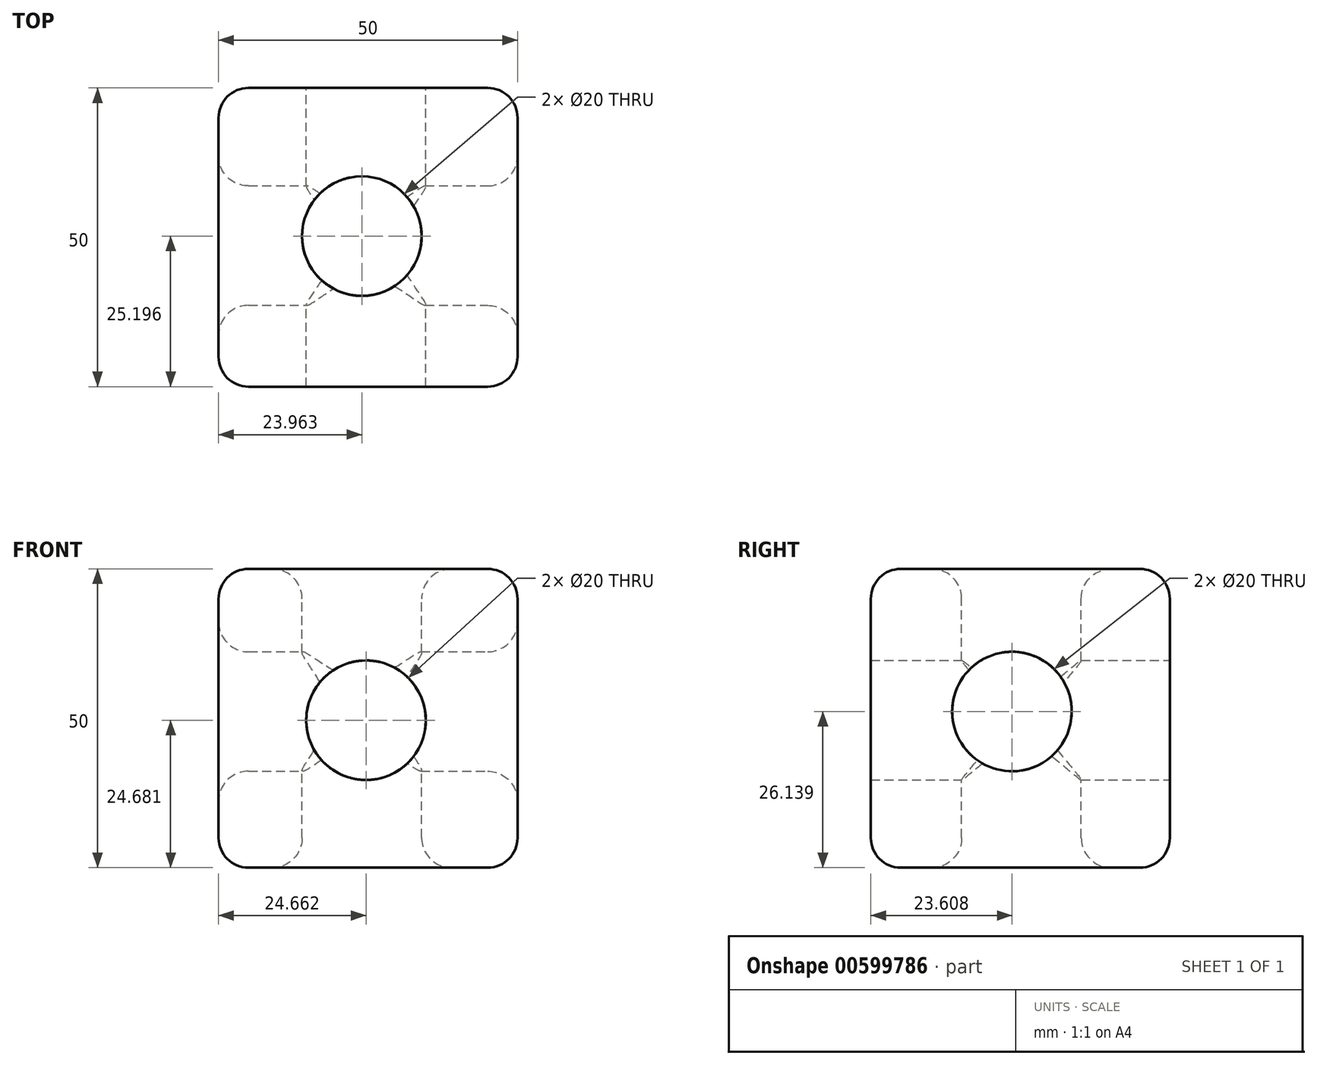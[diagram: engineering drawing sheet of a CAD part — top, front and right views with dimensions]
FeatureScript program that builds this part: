
annotation { "Feature Type Name" : "Feature", "Feature Type Description" : "" }
export const myFeature = defineFeature(function(context is Context, id is Id, definition is map)
    precondition{}
    {
        {
            var Q0;
            Q0=qCreatedBy(makeId("Top.planeOp"),FACE);
            var sketch = newSketch(context, id + "F0", { "sketchPlane" : qUnion([Q0])});
            skLineSegment(sketch, "E0.bottom", {"start": v(0, 0) * mm, "end": v(-50, 0) * mm});
            skLineSegment(sketch, "E0.top", {"start": v(0, -50) * mm, "end": v(-50, -50) * mm});
            skLineSegment(sketch, "E0.left", {"start": v(0, 0) * mm, "end": v(0, -50) * mm});
            skLineSegment(sketch, "E0.right", {"start": v(-50, 0) * mm, "end": v(-50, -50) * mm});
            skCircle(sketch, "E1", {"center": v(-26.04, -24.8) * mm, "radius": 10 * mm});
            skSolve(sketch);
        }
        {
            var Q0;
            Q0=makeQuery(id+"F0.imprint","IMPRINT",FACE,{"disambiguationData":[TD([[makeQuery(id+"F0.imprint","IMPRINT",EDGE,{"derivedFrom":sQuery(id+"F0.wireOp",EDGE,"E0.bottom")}),1.0]])]});
            extrude(context, id + "F1", {"entities" : qUnion([Q0]), "oppositeDirection" : true, "depth" : 50 * mm, "offsetDistance" : 25 * mm});
        }
        {
            var Q0;
            Q0=makeQuery(id+"F1.opExtrude","SWEPT_FACE",FACE,{"disambiguationData":[OSD([sQuery(id+"F0.wireOp",EDGE,"E0.bottom")])]});
            var sketch = newSketch(context, id + "F2", { "sketchPlane" : qUnion([Q0])});
            skCircle(sketch, "E2", {"center": v(25.34, -25.32) * mm, "radius": 10 * mm});
            skSolve(sketch);
        }
        {
            var Q0;
            Q0=sQuery(id+"F2.wireOp",VERTEX,"E2.center");
            var Q1;
            Q1=makeQuery(id+"F1.opExtrude","SWEPT_BODY",BODY,{"disambiguationData":[OSD([sQuery(id+"F0.wireOp",EDGE,"E0.bottom"),sQuery(id+"F0.wireOp",EDGE,"E0.top"),sQuery(id+"F0.wireOp",EDGE,"E0.left"),sQuery(id+"F0.wireOp",EDGE,"E0.right"),sQuery(id+"F0.wireOp",EDGE,"E1")])]});
            hole(context, id + "F3", {"style" : HoleStyle.SIMPLE, "endStyle" : HoleEndStyle.THROUGH, "holeDiameter" : 20 * mm, "majorDiameter" : 5 * mm, "isTappedThrough" : true, "tappedDepth" : 12.7 * mm, "tapClearance" : 3, "locations" : qUnion([Q0]), "scope" : qUnion([Q1])});
        }
        {
            var Q0;
            Q0=makeQuery(id+"F1.opExtrude","SWEPT_FACE",FACE,{"disambiguationData":[OSD([sQuery(id+"F0.wireOp",EDGE,"E0.left")])]});
            var sketch = newSketch(context, id + "F4", { "sketchPlane" : qUnion([Q0])});
            skCircle(sketch, "E3", {"center": v(-26.4, -23.86) * mm, "radius": 10 * mm});
            skSolve(sketch);
        }
        {
            var Q0;
            Q0=sQuery(id+"F4.wireOp",VERTEX,"E3.center");
            var Q1;
            Q1=makeQuery(id+"F1.opExtrude","SWEPT_BODY",BODY,{"disambiguationData":[OSD([sQuery(id+"F0.wireOp",EDGE,"E0.bottom"),sQuery(id+"F0.wireOp",EDGE,"E0.top"),sQuery(id+"F0.wireOp",EDGE,"E0.left"),sQuery(id+"F0.wireOp",EDGE,"E0.right"),sQuery(id+"F0.wireOp",EDGE,"E1")])]});
            hole(context, id + "F5", {"style" : HoleStyle.SIMPLE, "endStyle" : HoleEndStyle.THROUGH, "holeDiameter" : 20 * mm, "majorDiameter" : 5 * mm, "isTappedThrough" : true, "tappedDepth" : 12.7 * mm, "tapClearance" : 3, "locations" : qUnion([Q0]), "scope" : qUnion([Q1])});
        }
        {
            var Q0;
            Q0=makeQuery(id+"F1.opExtrude","CAP_FACE",FACE,{"disambiguationData":[OSD([sQuery(id+"F0.wireOp",EDGE,"E0.bottom"),sQuery(id+"F0.wireOp",EDGE,"E0.top"),sQuery(id+"F0.wireOp",EDGE,"E0.left"),sQuery(id+"F0.wireOp",EDGE,"E0.right"),sQuery(id+"F0.wireOp",EDGE,"E1")])],"isStart":true});
            var Q1;
            Q1=makeQuery(id+"F1.opExtrude","SWEPT_FACE",FACE,{"disambiguationData":[OSD([sQuery(id+"F0.wireOp",EDGE,"E0.right")])]});
            var Q2;
            Q2=makeQuery(id+"F1.opExtrude","CAP_FACE",FACE,{"disambiguationData":[OSD([sQuery(id+"F0.wireOp",EDGE,"E0.bottom"),sQuery(id+"F0.wireOp",EDGE,"E0.top"),sQuery(id+"F0.wireOp",EDGE,"E0.left"),sQuery(id+"F0.wireOp",EDGE,"E0.right"),sQuery(id+"F0.wireOp",EDGE,"E1")])],"isStart":false});
            var Q3;
            Q3=makeQuery(id+"F1.opExtrude","SWEPT_FACE",FACE,{"disambiguationData":[OSD([sQuery(id+"F0.wireOp",EDGE,"E0.left")])]});
            var Q4;
            Q4=makeQuery(id+"F3.hole-0.boolean.opBoolean","INTERSECT",EDGE,{"derivedFrom":[makeQuery(id+"F1.opExtrude","SWEPT_FACE",FACE,{"disambiguationData":[OSD([sQuery(id+"F0.wireOp",EDGE,"E0.top")])]}),makeQuery(id+"F3.hole-0.opRevolve","SWEPT_FACE",FACE,{"disambiguationData":[OSD([sQuery(id+"F3.hole-0.sketch.wireOp",EDGE,"core_line_2")])]})]});
            var Q5;
            Q5=makeQuery(id+"F5.hole-0.boolean.opBoolean","INTERSECT",EDGE,{"disambiguationData":[OD(3.0)],"derivedFrom":[makeQuery(id+"F3.hole-0.boolean.opBoolean","COPY",FACE,{"derivedFrom":makeQuery(id+"F3.hole-0.opRevolve","SWEPT_FACE",FACE,{"disambiguationData":[OSD([sQuery(id+"F3.hole-0.sketch.wireOp",EDGE,"core_line_2")])]})}),makeQuery(id+"F5.hole-0.opRevolve","SWEPT_FACE",FACE,{"disambiguationData":[OSD([sQuery(id+"F5.hole-0.sketch.wireOp",EDGE,"core_line_2")])]})]});
            var Q6;
            Q6=makeQuery(id+"F5.hole-0.boolean.opBoolean","INTERSECT",EDGE,{"disambiguationData":[OD(0.0)],"derivedFrom":[makeQuery(id+"F3.hole-0.boolean.opBoolean","COPY",FACE,{"derivedFrom":makeQuery(id+"F3.hole-0.opRevolve","SWEPT_FACE",FACE,{"disambiguationData":[OSD([sQuery(id+"F3.hole-0.sketch.wireOp",EDGE,"core_line_2")])]})}),makeQuery(id+"F5.hole-0.opRevolve","SWEPT_FACE",FACE,{"disambiguationData":[OSD([sQuery(id+"F5.hole-0.sketch.wireOp",EDGE,"core_line_2")])]})]});
            var Q7;
            Q7=makeQuery(id+"F5.hole-0.boolean.opBoolean","SPLIT",EDGE,{"disambiguationData":[OD(0.0)],"derivedFrom":makeQuery(id+"F3.hole-0.boolean.opBoolean","INTERSECT",EDGE,{"derivedFrom":[makeQuery(id+"F1.opExtrude","SWEPT_FACE",FACE,{"disambiguationData":[OSD([sQuery(id+"F0.wireOp",EDGE,"E1")])]}),makeQuery(id+"F3.hole-0.opRevolve","SWEPT_FACE",FACE,{"disambiguationData":[OSD([sQuery(id+"F3.hole-0.sketch.wireOp",EDGE,"core_line_2")])]})]})});
            var Q8;
            Q8=makeQuery(id+"F5.hole-0.boolean.opBoolean","INTERSECT",EDGE,{"disambiguationData":[OD(0.0)],"derivedFrom":[makeQuery(id+"F1.opExtrude","SWEPT_FACE",FACE,{"disambiguationData":[OSD([sQuery(id+"F0.wireOp",EDGE,"E1")])]}),makeQuery(id+"F5.hole-0.opRevolve","SWEPT_FACE",FACE,{"disambiguationData":[OSD([sQuery(id+"F5.hole-0.sketch.wireOp",EDGE,"core_line_2")])]})]});
            var Q9;
            Q9=makeQuery(id+"F5.hole-0.boolean.opBoolean","INTERSECT",EDGE,{"disambiguationData":[OD(2.0)],"derivedFrom":[makeQuery(id+"F3.hole-0.boolean.opBoolean","COPY",FACE,{"derivedFrom":makeQuery(id+"F3.hole-0.opRevolve","SWEPT_FACE",FACE,{"disambiguationData":[OSD([sQuery(id+"F3.hole-0.sketch.wireOp",EDGE,"core_line_2")])]})}),makeQuery(id+"F5.hole-0.opRevolve","SWEPT_FACE",FACE,{"disambiguationData":[OSD([sQuery(id+"F5.hole-0.sketch.wireOp",EDGE,"core_line_2")])]})]});
            var Q10;
            Q10=makeQuery(id+"F5.hole-0.boolean.opBoolean","INTERSECT",EDGE,{"disambiguationData":[OD(2.0)],"derivedFrom":[makeQuery(id+"F1.opExtrude","SWEPT_FACE",FACE,{"disambiguationData":[OSD([sQuery(id+"F0.wireOp",EDGE,"E1")])]}),makeQuery(id+"F5.hole-0.opRevolve","SWEPT_FACE",FACE,{"disambiguationData":[OSD([sQuery(id+"F5.hole-0.sketch.wireOp",EDGE,"core_line_2")])]})]});
            var Q11;
            Q11=makeQuery(id+"F3.hole-0.boolean.opBoolean","COPY",EDGE,{"derivedFrom":makeQuery(id+"F3.hole-0.opRevolve","SWEPT_EDGE",EDGE,{"disambiguationData":[OSD([sQuery(id+"F3.hole-0.sketch.wireOp",EDGE,"core_line_2"),sQuery(id+"F3.hole-0.sketch.wireOp",EDGE,"core_line_3")])]})});
            var Q12;
            Q12=makeQuery(id+"F5.hole-0.boolean.opBoolean","SPLIT",EDGE,{"disambiguationData":[OD(1.0)],"derivedFrom":makeQuery(id+"F3.hole-0.boolean.opBoolean","INTERSECT",EDGE,{"derivedFrom":[makeQuery(id+"F1.opExtrude","SWEPT_FACE",FACE,{"disambiguationData":[OSD([sQuery(id+"F0.wireOp",EDGE,"E1")])]}),makeQuery(id+"F3.hole-0.opRevolve","SWEPT_FACE",FACE,{"disambiguationData":[OSD([sQuery(id+"F3.hole-0.sketch.wireOp",EDGE,"core_line_2")])]})]})});
            var Q13;
            Q13=makeQuery(id+"F5.hole-0.boolean.opBoolean","INTERSECT",EDGE,{"disambiguationData":[OD(1.0)],"derivedFrom":[makeQuery(id+"F1.opExtrude","SWEPT_FACE",FACE,{"disambiguationData":[OSD([sQuery(id+"F0.wireOp",EDGE,"E1")])]}),makeQuery(id+"F5.hole-0.opRevolve","SWEPT_FACE",FACE,{"disambiguationData":[OSD([sQuery(id+"F5.hole-0.sketch.wireOp",EDGE,"core_line_2")])]})]});
            var Q14;
            Q14=makeQuery(id+"F5.hole-0.boolean.opBoolean","INTERSECT",EDGE,{"disambiguationData":[OD(3.0)],"derivedFrom":[makeQuery(id+"F1.opExtrude","SWEPT_FACE",FACE,{"disambiguationData":[OSD([sQuery(id+"F0.wireOp",EDGE,"E1")])]}),makeQuery(id+"F5.hole-0.opRevolve","SWEPT_FACE",FACE,{"disambiguationData":[OSD([sQuery(id+"F5.hole-0.sketch.wireOp",EDGE,"core_line_2")])]})]});
            fillet(context, id + "F6", {"entities" : qUnion([Q0, Q1, Q2, Q3, Q4, Q5, Q6, Q7, Q8, Q9, Q10, Q11, Q12, Q13, Q14]), "radius" : 5 * mm, "tangentPropagation" : true, "allowEdgeOverflow" : false});
        }
    });
